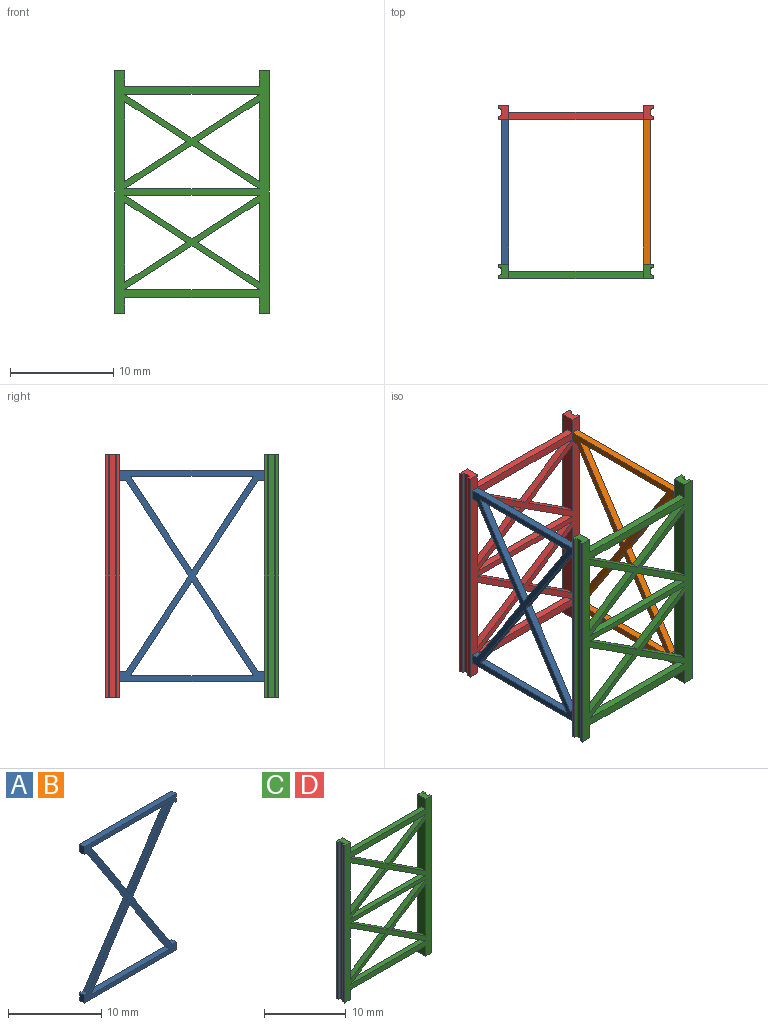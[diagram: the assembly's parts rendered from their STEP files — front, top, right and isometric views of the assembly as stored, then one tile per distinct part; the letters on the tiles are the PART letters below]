
ASSEMBLY  parts=4 mates=3
PART A: 22 faces, bbox 14x0.7x20.5 mm
  f0: plane 9.1x5.94mm, normal (0.84,0,0.55), area 7.6mm2, adj f1,f19,f20,f21
  f1: plane 11.89x0.7mm, normal (0,0,-1), area 8.3mm2, adj f0,f19,f20,f21
  f2: plane 11.89x0.7mm, normal (0,0,1), area 8.3mm2, adj f3,f17,f20,f21
  f3: plane 9.1x5.94mm, normal (0.84,0,-0.55), area 7.6mm2, adj f2,f17,f20,f21
  f4: plane 1x0.7mm, normal (-1,0,0), area 0.7mm2, adj f5,f18,f20,f21
  f5: plane 0.7x0.6mm, normal (0,0,-1), area 0.4mm2, adj f4,f6,f20,f21
  f6: plane 9.25x6.04mm, normal (-0.84,0,-0.55), area 7.7mm2, adj f5,f7,f20,f21
  f7: plane 9.25x6.04mm, normal (-0.84,0,0.55), area 7.7mm2, adj f6,f8,f20,f21
  f8: plane 0.7x0.6mm, normal (0,0,1), area 0.4mm2, adj f7,f9,f20,f21
  f9: plane 1x0.7mm, normal (-1,0,0), area 0.7mm2, adj f8,f10,f20,f21
  f10: plane 14x0.7mm, normal (0,0,-1), area 9.8mm2, adj f9,f11,f20,f21
  f11: plane 1x0.7mm, normal (1,0,0), area 0.7mm2, adj f10,f12,f20,f21
  f12: plane 0.7x0.6mm, normal (0,0,1), area 0.4mm2, adj f11,f13,f20,f21
  f13: plane 9.25x6.04mm, normal (0.84,0,0.55), area 7.7mm2, adj f12,f14,f20,f21
  f14: plane 9.25x6.04mm, normal (0.84,0,-0.55), area 7.7mm2, adj f13,f15,f20,f21
  f15: plane 0.7x0.6mm, normal (0,0,-1), area 0.4mm2, adj f14,f16,f20,f21
  f16: plane 1x0.7mm, normal (1,0,0), area 0.7mm2, adj f15,f18,f20,f21
  f17: plane 9.1x5.94mm, normal (-0.84,0,-0.55), area 7.6mm2, adj f2,f3,f20,f21
  f18: plane 14x0.7mm, normal (0,0,1), area 9.8mm2, adj f4,f16,f20,f21
  f19: plane 9.1x5.94mm, normal (-0.84,0,0.55), area 7.6mm2, adj f0,f1,f20,f21
  f20: plane 20.5x14mm, normal (0,-1,0), area 44.8mm2, adj f0,f1,f2,f3,f4,f5,f6,f7
  f21: plane 20.5x14mm, normal (0,1,0), area 44.8mm2, adj f0,f1,f2,f3,f4,f5,f6,f7
PART B: same geometry as A
PART C: 46 faces, bbox 15x1.4x23.5 mm
  f0: plane 23.5x0.3mm, normal (1,0,0), area 7mm2, adj f16,f18,f38,f44
  f1: plane 23.5x0.3mm, normal (-1,0,0), area 7mm2, adj f2,f3,f39,f42
  f2: plane 1.4x1mm, normal (0,0,1), area 1.2mm2, adj f1,f20,f21,f37,f39,f40,f41,f42
  f3: plane 1.4x1mm, normal (0,0,-1), area 1.2mm2, adj f1,f20,f21,f37,f39,f40,f41,f42
  f4: plane 13x0.8mm, normal (0,1,0), area 10.4mm2, adj f10,f12,f19,f21
  f5: plane 13x9.15mm, normal (0,1,0), area 18.2mm2, adj f9,f11,f12,f21,f26,f28,f29,f34
  f6: plane 13x0.6mm, normal (0,1,0), area 7.8mm2, adj f12,f14,f21,f27
  f7: plane 13x9.15mm, normal (0,1,0), area 18.2mm2, adj f12,f13,f15,f21,f23,f25,f30,f31
  f8: plane 13x0.8mm, normal (0,1,0), area 10.4mm2, adj f12,f21,f22,f24
  f9: plane 6.5x4.22mm, normal (0.54,0,0.84), area 5.4mm2, adj f5,f10,f36,f37
  f10: plane 13x0.7mm, normal (0,0,-1), area 9.1mm2, adj f4,f9,f36,f37
  f11: plane 5.95x3.86mm, normal (0.54,0,-0.84), area 5mm2, adj f5,f12,f29,f37
  f12: plane 23.5x1.4mm, normal (-1,0,0), area 29.4mm2, adj f4,f5,f6,f7,f8,f11,f15,f16
  f13: plane 6.5x4.22mm, normal (0.54,0,0.84), area 5.4mm2, adj f7,f14,f30,f37
  f14: plane 13x0.7mm, normal (0,0,-1), area 9.1mm2, adj f6,f13,f30,f37
  f15: plane 5.95x3.86mm, normal (0.54,0,-0.84), area 5mm2, adj f7,f12,f31,f37
  f16: plane 1.4x1mm, normal (0,0,-1), area 1.2mm2, adj f0,f12,f17,f37,f38,f43,f44,f45
  f17: plane 23.5x0.3mm, normal (1,0,0), area 7mm2, adj f16,f18,f37,f43
  f18: plane 1.4x1mm, normal (0,0,1), area 1.2mm2, adj f0,f12,f17,f37,f38,f43,f44,f45
  f19: plane 13x0.7mm, normal (0,0,1), area 9.1mm2, adj f4,f12,f21,f37
  f20: plane 23.5x0.3mm, normal (-1,0,0), area 7mm2, adj f2,f3,f37,f40
  f21: plane 23.5x1.4mm, normal (1,0,0), area 29.4mm2, adj f2,f3,f4,f5,f6,f7,f8,f19
  f22: plane 13x0.7mm, normal (0,0,-1), area 9.1mm2, adj f8,f12,f21,f37
  f23: plane 5.95x3.86mm, normal (-0.54,0,-0.84), area 5mm2, adj f7,f21,f32,f37
  f24: plane 13x0.7mm, normal (0,0,1), area 9.1mm2, adj f8,f25,f33,f37
  f25: plane 6.5x4.22mm, normal (0.54,0,-0.84), area 5.4mm2, adj f7,f24,f33,f37
  f26: plane 5.95x3.86mm, normal (-0.54,0,-0.84), area 5mm2, adj f5,f21,f34,f37
  f27: plane 13x0.7mm, normal (0,0,1), area 9.1mm2, adj f6,f28,f35,f37
  f28: plane 6.5x4.22mm, normal (0.54,0,-0.84), area 5.4mm2, adj f5,f27,f35,f37
  f29: plane 5.95x3.86mm, normal (0.54,0,0.84), area 5mm2, adj f5,f11,f12,f37
  f30: plane 6.5x4.22mm, normal (-0.54,0,0.84), area 5.4mm2, adj f7,f13,f14,f37
  f31: plane 5.95x3.86mm, normal (0.54,0,0.84), area 5mm2, adj f7,f12,f15,f37
  f32: plane 5.95x3.86mm, normal (-0.54,0,0.84), area 5mm2, adj f7,f21,f23,f37
  f33: plane 6.5x4.22mm, normal (-0.54,0,-0.84), area 5.4mm2, adj f7,f24,f25,f37
  f34: plane 5.95x3.86mm, normal (-0.54,0,0.84), area 5mm2, adj f5,f21,f26,f37
  f35: plane 6.5x4.22mm, normal (-0.54,0,-0.84), area 5.4mm2, adj f5,f27,f28,f37
  f36: plane 6.5x4.22mm, normal (-0.54,0,0.84), area 5.4mm2, adj f5,f9,f10,f37
  f37: plane 23.5x15mm, normal (0,-1,0), area 112mm2, adj f2,f3,f9,f10,f11,f12,f13,f14
  f38: plane 23.5x1mm, normal (0,1,0), area 23.5mm2, adj f0,f12,f16,f18
  f39: plane 23.5x1mm, normal (0,1,0), area 23.5mm2, adj f1,f2,f3,f21
  f40: plane 23.5x0.3mm, normal (-0.26,0.97,0), area 7.3mm2, adj f2,f3,f20,f41
  f41: plane 23.5x0.64mm, normal (-1,0,0), area 15mm2, adj f2,f3,f40,f42
  f42: plane 23.5x0.3mm, normal (-0.26,-0.97,0), area 7.3mm2, adj f1,f2,f3,f41
  f43: plane 23.5x0.3mm, normal (0.26,0.97,0), area 7.3mm2, adj f16,f17,f18,f45
  f44: plane 23.5x0.3mm, normal (0.26,-0.97,0), area 7.3mm2, adj f0,f16,f18,f45
  f45: plane 23.5x0.64mm, normal (1,0,0), area 15mm2, adj f16,f18,f43,f44
PART D: same geometry as C
PLACE A rot(axis=(0,0,1),90deg) t=(0.3,1.4,1.5)mm
PLACE B rot(axis=(0,0,-1),90deg) t=(14.7,15.4,1.5)mm
PLACE C t=(0,0.7,1.5)mm
PLACE D rot(axis=(1,0,0),0deg) t=(0,16.1,1.5)mm
MATE fastened B.f16 <-> C.f38  axis (0,-1,0) through (14.7,1.4,22)mm
MATE fastened C.f39 <-> A.f4  axis (0,1,0) through (0,1.4,22)mm
MATE fastened D.f37 <-> B.f4  axis (0,-1,0) through (15,15.4,22)mm
